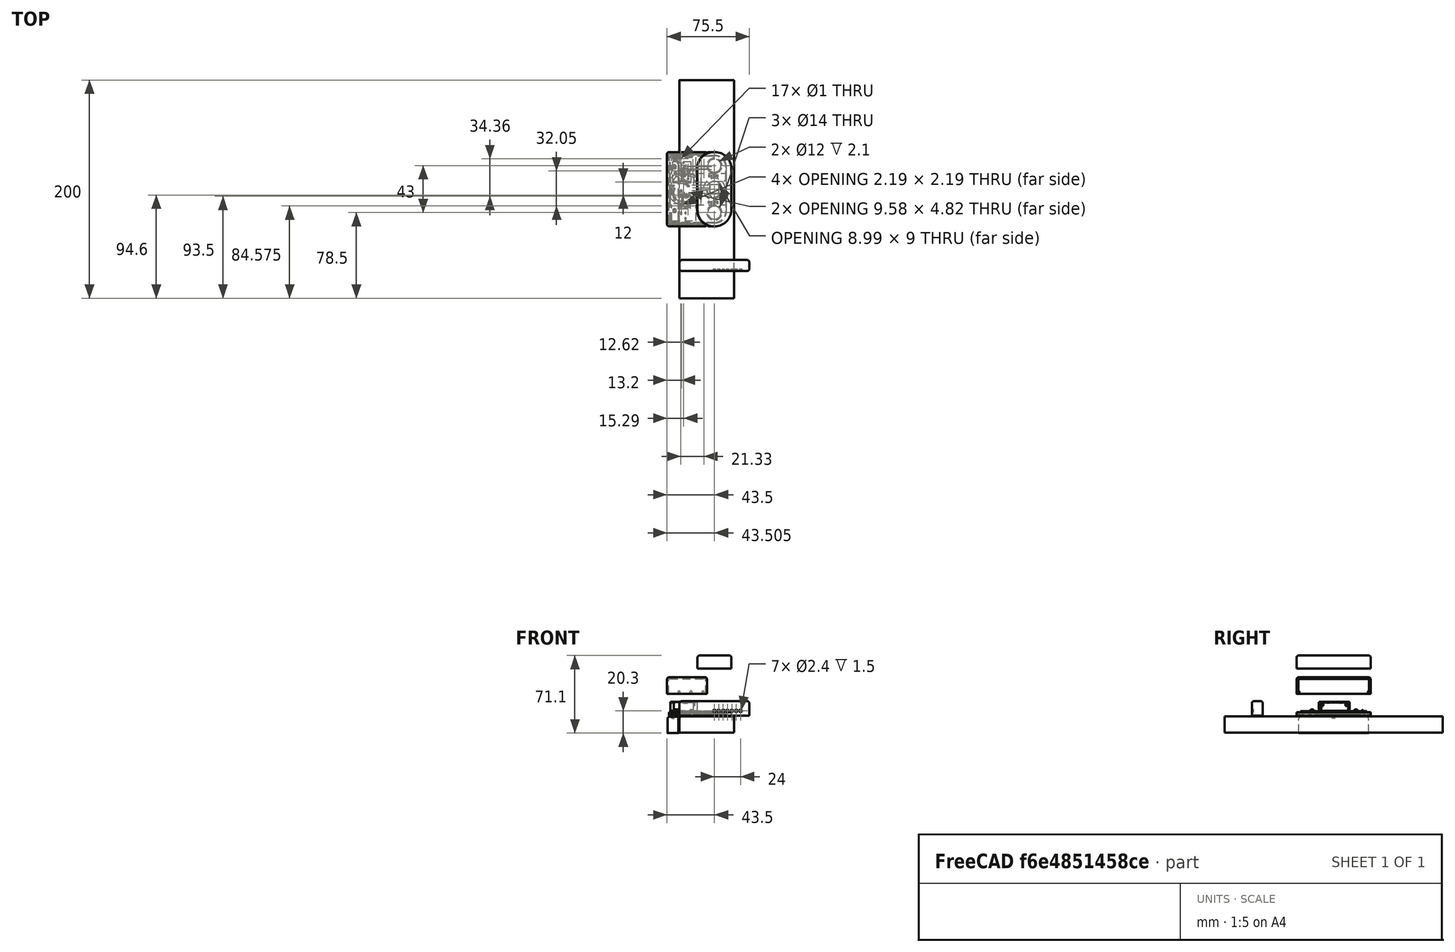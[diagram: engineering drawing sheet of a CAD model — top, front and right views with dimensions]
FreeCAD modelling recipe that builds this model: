
FCSTD DOCUMENT  (FreeCAD 0.18R4 (GitTag))
Label: RHS_3
License: All rights reserved
LicenseURL: http://en.wikipedia.org/wiki/All_rights_reserved
objects: Part::Box×15, Part::Cylinder×13, Part::Cut×13, Part::Fillet×11, Part::FeaturePython×9, Part::MultiFuse×7, Part::Sphere×2, Part::Torus×1, Part::Feature×1, Spreadsheet::Sheet×1
note: 72 computed .brp shape members not serialized (recipe doc carries the construction recipe); baked Part::Feature solids carry a one-line shape summary decoded from their .brp

FEATURE [Part::Box] Box014  label="Würfel003"
  AttacherType = Attacher::AttachEngine3D
  Height = 15
  Length = 64
  Placement = pos=(-32,-55,-1.4) rot=(0,0,1;0rad)
  Width = 10
  expr: Placement.Base.y = -Width / 2 - 50mm
  expr: Placement.Base.x = -Length / 2
FEATURE [Part::Cylinder] Cylinder004  label="Zylinder002"
  Angle = 360
  AttacherType = Attacher::AttachEngine3D
  Height = 1.8
  Placement = pos=(0,-50,11.9) rot=(0,0,1;0rad)
  Radius = 1.2
  expr: Placement.Base.z = 12.9 - 1
FEATURE [Part::FeaturePython] Array006  # Draft array (typed FeaturePython)
  Angle = 360
  ArrayType = 0
  Axis = (0,0,1)
  Base = -> Cylinder004
  Center = (0,0,0)
  Fuse = false
  IntervalAxis = (0,0,0)
  IntervalX = (4,0,0)
  IntervalY = (0,1,0)
  IntervalZ = (0,0,0)
  NumberPolar = 1
  NumberX = 1
  NumberY = 1
  NumberZ = 1
FEATURE [Part::Fillet] Fillet005
  Base = -> Box014
  Edges = 8 edges r=2: [Edge1,Edge2,Edge3,Edge5,Edge6,Edge7,Edge10,Edge12]
FEATURE [Part::Cut] Cut009  label="Unterteil"
  Base = -> Fillet005
  Placement = pos=(-88,0,-16) rot=(0,0,1;1.5708rad)
  Tool = -> Array006
  expr: Placement.Base.z = FBox.Placement.Base.z + 1mm
FEATURE [Part::Box] Box015  label="Würfel004"
  AttacherType = Attacher::AttachEngine3D
  Height = 13.2
  Length = 64
  Placement = pos=(-32,-75,-1.4) rot=(0,0,1;0rad)
  Width = 10
  expr: Placement.Base.z = Würfel003.Placement.Base.z
  expr: Height = 13.2mm
  expr: Placement.Base.y = Würfel003.Placement.Base.y - 20mm
  expr: Placement.Base.x = Würfel003.Placement.Base.x
  expr: Width = Würfel003.Width
  expr: Length = Würfel003.Length
FEATURE [Part::Cylinder] Cylinder005  label="Zylinder003"
  Angle = 360
  AttacherType = Attacher::AttachEngine3D
  Height = 1.8
  Placement = pos=(0,-73.5,2.9) rot=(1,0,0;1.5708rad)
  Radius = 1.2
  expr: Placement.Base.z = Zylinder002.Placement.Base.z - 9mm
  expr: Height = Zylinder002.Height
  expr: Placement.Base.y = Würfel004.Placement.Base.y + 1.5mm
  expr: Placement.Base.x = Zylinder002.Placement.Base.x
  expr: Radius = Zylinder002.Radius
FEATURE [Part::Fillet] Fillet006
  Base = -> Box015
  Edges = 8 edges r=2: [Edge1,Edge2,Edge3,Edge5,Edge6,Edge7,Edge10,Edge12]
FEATURE [Part::FeaturePython] Array007  # Draft array (typed FeaturePython)
  Angle = 360
  ArrayType = 0
  Axis = (0,0,1)
  Base = -> Cylinder005
  Center = (0,0,0)
  Fuse = false
  IntervalAxis = (0,0,0)
  IntervalX = (4,0,0)
  IntervalY = (0,1,0)
  IntervalZ = (0,0,0)
  NumberPolar = 1
  NumberX = 7
  NumberY = 1
  NumberZ = 1
FEATURE [Part::Cut] Cut010  label="Seitenteil"
  Base = -> Fillet006
  Tool = -> Array007
FEATURE [Part::Box] Box016  label="Vierkant"
  AttacherType = Attacher::AttachEngine3D
  Height = 10
  Length = 8
  Placement = pos=(-4,-4,-2) rot=(0,0,1;0rad)
  Width = 8
  expr: Placement.Base.y = -Width / 2
  expr: Placement.Base.x = -Length / 2
FEATURE [Part::Cylinder] Cylinder012  label="MagHoldBase"
  Angle = 360
  AttacherType = Attacher::AttachEngine3D
  Height = 2.4
  Radius = 7.7
  expr: Height = Parameter.Pcb_Height + 1.4mm
FEATURE [Part::Cylinder] Cylinder003  label="MagHoldTop"
  Angle = 360
  AttacherType = Attacher::AttachEngine3D
  Height = 1.4
  Radius = 10
  expr: Placement.Base.z = 0
FEATURE [Part::Cylinder] Cylinder013  label="Cylinder012"
  Angle = 360
  AttacherType = Attacher::AttachEngine3D
  Height = 10
  Placement = pos=(4,4,-2) rot=(0,0,1;0rad)
  Radius = 0.5
  expr: Placement.Base.y = Vierkant.Width / 2
  expr: Placement.Base.x = Vierkant.Length / 2
FEATURE [Part::FeaturePython] Array013  # Draft array (typed FeaturePython)
  Angle = 360
  ArrayType = 0
  Axis = (0,0,1)
  Base = -> Cylinder013
  Center = (0,0,0)
  Fuse = false
  IntervalAxis = (0,0,0)
  IntervalX = (-8,0,0)
  IntervalY = (0,-8,0)
  IntervalZ = (0,0,1)
  NumberPolar = 1
  NumberX = 2
  NumberY = 2
  NumberZ = 1
  expr: IntervalY.y = -Vierkant.Width
  expr: IntervalX.x = -Vierkant.Length
FEATURE [Part::Cylinder] Cylinder014  label="Magnet"
  Angle = 360
  AttacherType = Attacher::AttachEngine3D
  Height = 3
  Placement = pos=(0,-8.5,-1) rot=(0,0,1;0rad)
  Radius = 1.2
  expr: Placement.Base.z = MagHoldTop.Placement.Base.z - 1mm
  expr: Placement.Base.y = -MagHoldTop.Radius + 1.5mm
FEATURE [Part::Torus] Torus
  Angle1 = -180
  Angle2 = 180
  Angle3 = 360
  AttacherType = Attacher::AttachEngine3D
  Placement = pos=(0,0,1.9) rot=(0,0,1;0rad)
  Radius1 = 7.7
  Radius2 = 0.7
  expr: Radius1 = MagHoldBase.Radius
FEATURE [Part::Cut] Cut017
  Base = -> Cylinder012
  Tool = -> Torus
FEATURE [Part::MultiFuse] Fusion003
  Shapes = -> [Cylinder003,Cut017]
FEATURE [Part::Cut] Cut018
  Base = -> Fusion003
  Tool = -> Box016
FEATURE [Part::Cut] Cut019
  Base = -> Cut018
  Tool = -> Array013
FEATURE [Part::Cut] Cut020  label="MagnetHalter"
  Base = -> Cut019
  Tool = -> Cylinder014
  expr: Placement.Base.z = 0mm + 0mm
FEATURE [Part::Box] Box018  label="Cube"
  AttacherType = Attacher::AttachEngine3D
  Height = 12
  Length = 31
  Placement = pos=(-15.5,-34,1.7) rot=(0,0,1;0rad)
  Width = 68
  expr: Length = Parameter.GriffR_Width
  expr: Width = Parameter.GriffR_Height
  expr: Placement.Base.z = ERO.Placement.Base.z + ERO.Height
  expr: Placement.Base.y = -Width / 2
  expr: Placement.Base.x = -Length / 2
FEATURE [Part::Fillet] Fillet010  label="GriffBaseR"
  Base = -> Box018
  Edges = 4 edges r=15: [Edge1,Edge3,Edge5,Edge7]
FEATURE [Part::Fillet] Fillet011  label="GriffR"
  Base = -> Fillet010
  Edges = 8 edges r=2: [Edge1,Edge5,Edge6,Edge7,Edge8,Edge9,Edge10,Edge11]
  Placement = pos=(0,0,40) rot=(0,0,1;0rad)
FEATURE [Part::Box] Box019  label="DBlockR"
  AttacherType = Attacher::AttachEngine3D
  Height = 15.1
  Length = 37
  Placement = pos=(-43.5,-34,-1.4) rot=(0,0,1;0rad)
  Width = 68
  expr: Height = ERO.Height + 12mm
  expr: Placement.Base.z = ERO.Placement.Base.z
  expr: Placement.Base.y = -Width / 2
  expr: Placement.Base.x = RR.Placement.Base.x
  expr: Width = Parameter.GriffR_Height
FEATURE [Part::FeaturePython] Clone003  label="GriffBaseRForCut"  # Draft clone (typed FeaturePython)
  AttacherType = Attacher::AttachEngine3D
  Fuse = false
  Objects = -> [Fillet010]
  Placement = pos=(0,0,-5) rot=(0,0,1;0rad)
  Scale = (1.02,1.01,1.8)
FEATURE [Part::Fillet] Fillet012
  Base = -> Box019
  Edges = 8 edges r=2: [Edge1,Edge2,Edge3,Edge5,Edge6,Edge7,Edge10,Edge12]
FEATURE [Part::Cut] Cut024
  Base = -> Fillet012
  Tool = -> Clone003
FEATURE [Part::Box] Box020  label="DBlockRCutout"
  AttacherType = Attacher::AttachEngine3D
  Height = 13.5
  Length = 37
  Placement = pos=(-41.9,-32.4,-1.4) rot=(0,0,1;0rad)
  Width = 64.8
  expr: Placement.Base.y = -Width / 2
  expr: Placement.Base.x = DBlockR.Placement.Base.x + Parameter.Wall_Width
  expr: Placement.Base.z = DBlockR.Placement.Base.z
  expr: Height = DBlockR.Height - Parameter.Wall_Width
  expr: Width = DBlockR.Width - Parameter.Wall_Width - Parameter.Wall_Width
  expr: Length = DBlockR.Length
FEATURE [Part::Fillet] Fillet013
  Base = -> Box020
  Edges = 2 edges r=1: [Edge1,Edge3]
FEATURE [Part::Cut] Cut025
  Base = -> Cut024
  Tool = -> Fillet013
FEATURE [Part::Cylinder] Cylinder017  label="CR2477"
  Angle = 360
  AttacherType = Attacher::AttachEngine3D
  Height = 7.7
  Placement = pos=(-28,1,3) rot=(0,0,1;0rad)
  Radius = 12.25
  expr: Placement.Base.z = PlatineV_1_1.Placement.Base.z + 0.4mm
FEATURE [Part::Box] Box021  label="FBox"
  AttacherType = Attacher::AttachEngine3D
  Height = 15
  Length = 50
  Placement = pos=(-32,-100,-17) rot=(0,0,1;0rad)
  Width = 200
  expr: Placement.Base.z = -Height - 2mm
  expr: Placement.Base.x = -32
  expr: Placement.Base.y = -Width / 2
FEATURE [Part::Fillet] Fillet015  label="FensterRahmen"
  Base = -> Box021
  Edges = 1 edges r=2: [Edge2]
FEATURE [Part::Feature] RHS_3_cp_cp002  label="PlatineV_1_1"
  Placement = pos=(-100,100,2.6) rot=(0,0,1;0rad)
  shape: bbox 51 x 61 x 11.72 mm, 3088 faces, 33 solids (baked)
  expr: Placement.Base.z = 2.6mm + 0mm
FEATURE [Spreadsheet::Sheet] Spreadsheet  label="Parameter"
  cells = A3=Griff Rund; A4=Höhe; B4(GriffR_Height)==68mm; A5=Breite; B5(GriffR_Width)==31mm; C5=Rundung muss bei GriffBaseR angepasst werden; A8=Platine; A9=Dicke; B9(Pcb_Height)==1mm; A10=Bauteilhöhe; B10(Part_Height)==1.5mm; A11=Breite; B11(Pcb_Width)==51mm; A12=Länge; B12(Pcb_Length)==61mm; A13=Radius; B13(Pcb_Radius)==10.5mm; A15=Deckel; A16=Wandstärke; B16(Wall_Width)==1.6mm
FEATURE [Part::Cylinder] Cylinder018  label="ERO"
  Angle = 90
  AttacherType = Attacher::AttachEngine3D
  Height = 3.1
  Placement = pos=(0,18.5,-1.4) rot=(0,0,1;0rad)
  Radius = 15.5
  expr: Height = Parameter.Pcb_Height + Parameter.Part_Height + 0.6mm
  expr: Placement.Base.y = Parameter.GriffR_Height / 2 - Radius
  expr: Radius = Parameter.GriffR_Width / 2
FEATURE [Part::Cylinder] Cylinder019  label="ERU"
  Angle = 90
  AttacherType = Attacher::AttachEngine3D
  Height = 3.1
  Placement = pos=(0,-18.5,-1.4) rot=(0,0,-1;1.5708rad)
  Radius = 15.5
  expr: Placement.Base.z = ERO.Placement.Base.z
  expr: Height = ERO.Height
  expr: Placement.Base.y = -ERO.Placement.Base.y
  expr: Radius = ERO.Radius
FEATURE [Part::Box] Box024  label="MR"
  AttacherType = Attacher::AttachEngine3D
  Height = 3.1
  Length = 15.5
  Placement = pos=(0,-18.5,-1.4) rot=(0,0,1;0rad)
  Width = 37
  expr: Placement.Base.y = -Width / 2
  expr: Placement.Base.z = ERO.Placement.Base.z
  expr: Height = ERO.Height
  expr: Width = Parameter.GriffR_Height - Parameter.GriffR_Width
  expr: Length = ERO.Radius
FEATURE [Part::Box] Box025  label="RR"
  AttacherType = Attacher::AttachEngine3D
  Height = 3.1
  Length = 43.5
  Placement = pos=(-43.5,-34,-1.4) rot=(0,0,1;0rad)
  Width = 68
  expr: Width = Parameter.GriffR_Height
  expr: Placement.Base.z = ERO.Placement.Base.z
  expr: Height = ERO.Height
  expr: Placement.Base.y = -Width / 2
  expr: Placement.Base.x = -Length
  expr: Length = Parameter.Pcb_Width - Parameter.Pcb_Radius + 3mm
FEATURE [Part::Fillet] Fillet017
  Base = -> Box025
  Edges = 2 edges r=2: [Edge1,Edge3]
FEATURE [Part::MultiFuse] Fusion007  label="GPR"
  Shapes = -> [Cylinder018,Cylinder019,Box024,Fillet017]
FEATURE [Part::Box] Box026  label="PlatineCut"
  AttacherType = Attacher::AttachEngine3D
  Height = 1
  Length = 52
  Placement = pos=(-41,-31,0.7) rot=(0,0,1;0rad)
  Width = 62
  expr: Placement.Base.x = RR.Placement.Base.x + 2.5mm
  expr: Placement.Base.y = -Width / 2
  expr: Placement.Base.z = ERO.Placement.Base.z + ERO.Height - Height
  expr: Height = Parameter.Pcb_Height
FEATURE [Part::Fillet] Fillet018
  Base = -> Box026
  Edges = 2 edges r=2.5: [Edge1,Edge3]
FEATURE [Part::Fillet] Fillet019
  Base = -> Fillet018
  Edges = 2 edges r=10.5: [Edge17,Edge18]
FEATURE [Part::Cut] Cut030
  Base = -> Fusion007
  Tool = -> Fillet019
FEATURE [Part::Box] Box027  label="PartCut1"
  AttacherType = Attacher::AttachEngine3D
  Height = 1.5
  Length = 52
  Placement = pos=(-41,-14.5,-0.8) rot=(0,0,1;0rad)
  Width = 29
  expr: Placement.Base.y = -Width / 2
  expr: Placement.Base.x = PlatineCut.Placement.Base.x
  expr: Length = PlatineCut.Length
  expr: Placement.Base.z = PlatineCut.Placement.Base.z - Height
  expr: Height = Parameter.Part_Height
FEATURE [Part::Box] Box028  label="PartCut2"
  AttacherType = Attacher::AttachEngine3D
  Height = 1.5
  Length = 22
  Placement = pos=(-39,-29,-0.8) rot=(0,0,1;0rad)
  Width = 58
  expr: Placement.Base.y = -Width / 2
  expr: Placement.Base.x = PartCut1.Placement.Base.x + 2mm
  expr: Placement.Base.z = PartCut1.Placement.Base.z
  expr: Height = PartCut1.Height
FEATURE [Part::MultiFuse] Fusion008  label="PartCuts"
  Shapes = -> [Box027,Box028]
FEATURE [Part::Cut] Cut031
  Base = -> Cut030
  Tool = -> Fusion008
FEATURE [Part::Cylinder] Cylinder020  label="LochU"
  Angle = 360
  AttacherType = Attacher::AttachEngine3D
  Height = 10
  Placement = pos=(0,-21.5,-3) rot=(0,0,1;0rad)
  Radius = 6
FEATURE [Part::Cylinder] Cylinder021  label="LochO"
  Angle = 360
  AttacherType = Attacher::AttachEngine3D
  Height = 10
  Placement = pos=(0,21.5,-3) rot=(0,0,1;0rad)
  Radius = 6
  expr: Placement.Base.y = -LochU.Placement.Base.y
  expr: Placement.Base.z = LochU.Placement.Base.z
FEATURE [Part::Cylinder] Cylinder022  label="LochM"
  Angle = 360
  AttacherType = Attacher::AttachEngine3D
  Height = 10
  Placement = pos=(0,0,-3) rot=(0,0,1;0rad)
  Radius = 7
  expr: Placement.Base.z = LochU.Placement.Base.z
FEATURE [Part::MultiFuse] Fusion009  label="LochOMU"
  Shapes = -> [Cylinder020,Cylinder021,Cylinder022]
FEATURE [Part::Cut] Cut032
  Base = -> Cut031
  Tool = -> Fusion009
FEATURE [Part::Box] Box029  label="DBCut"
  AttacherType = Attacher::AttachEngine3D
  Height = 10
  Length = 37
  Placement = pos=(-43.5,-34,-1.4) rot=(0,0,1;0rad)
  Width = 1.8
  expr: Width = Parameter.Wall_Width + 0.2mm
  expr: Placement.Base.z = DBlockR.Placement.Base.z
  expr: Placement.Base.y = DBlockR.Placement.Base.y
  expr: Placement.Base.x = DBlockR.Placement.Base.x
  expr: Length = DBlockR.Length
FEATURE [Part::FeaturePython] Array016  # Draft array (typed FeaturePython)
  Angle = 360
  ArrayType = 0
  Axis = (0,0,1)
  Base = -> Box029
  Center = (0,0,0)
  Fuse = false
  IntervalAxis = (0,0,0)
  IntervalX = (1,0,0)
  IntervalY = (0,66.2,0)
  IntervalZ = (0,0,1)
  NumberPolar = 1
  NumberX = 1
  NumberY = 2
  NumberZ = 1
  expr: IntervalY.y = DBlockR.Width - DBCut.Width
FEATURE [Part::Box] Box030  label="DBCut2"
  AttacherType = Attacher::AttachEngine3D
  Height = 10
  Length = 1.8
  Placement = pos=(-43.5,-34,-1.4) rot=(0,0,1;0rad)
  Width = 68
  expr: Placement.Base.z = DBlockR.Placement.Base.z
  expr: Placement.Base.y = DBlockR.Placement.Base.y
  expr: Placement.Base.x = DBlockR.Placement.Base.x
  expr: Width = DBlockR.Width
  expr: Length = DBCut.Width
FEATURE [Part::MultiFuse] Fusion012  label="DeckelRandCut"
  Shapes = -> [Array016,Box030]
FEATURE [Part::Cut] Cut033
  Base = -> Cut032
  Tool = -> Fusion012
FEATURE [Part::Fillet] Fillet020
  Base = -> Cut033
  Edges = 4 edges r=1: [Edge12,Edge91,Edge93,Edge94]
FEATURE [Part::Sphere] Sphere  label="Fed0"
  Angle1 = -90
  Angle2 = 90
  Angle3 = 360
  AttacherType = Attacher::AttachEngine3D
  Placement = pos=(-10.5,-32.4,0.2) rot=(0,0,1;0rad)
  Radius = 1
  expr: Placement.Base.z = DBlockR.Placement.Base.z + Radius + 0.6mm
  expr: Placement.Base.x = DBlockR.Placement.Base.x + DBlockR.Length - 4mm
  expr: Placement.Base.y = DBlockR.Placement.Base.y + Parameter.Wall_Width
FEATURE [Part::FeaturePython] Array  label="FedAll"  # Draft array (typed FeaturePython)
  Angle = 360
  ArrayType = 0
  Axis = (0,0,1)
  Base = -> Sphere
  Center = (0,0,0)
  Fuse = false
  IntervalAxis = (0,0,0)
  IntervalX = (-11,0,0)
  IntervalY = (0,64.8,0)
  IntervalZ = (0,0,1)
  NumberPolar = 1
  NumberX = 3
  NumberY = 2
  NumberZ = 1
  expr: IntervalY.y = DBlockRCutout.Width
FEATURE [Part::MultiFuse] Fusion  label="DeckelR"
  Placement = pos=(0,0,20) rot=(0,0,1;0rad)
  Shapes = -> [Cut025,Array]
FEATURE [Part::Sphere] Sphere001  label="Nut0"
  Angle1 = -90
  Angle2 = 90
  Angle3 = 360
  AttacherType = Attacher::AttachEngine3D
  Placement = pos=(-10.5,-32.4,0.2) rot=(0,0,1;0rad)
  Radius = 1.1
  expr: Placement.Base.z = Fed0.Placement.Base.z
  expr: Placement.Base.y = Fed0.Placement.Base.y
  expr: Placement.Base.x = Fed0.Placement.Base.x
  expr: Radius = Fed0.Radius + 0.1mm
FEATURE [Part::FeaturePython] Array017  label="Nut01"  # Draft array (typed FeaturePython)
  Angle = 360
  ArrayType = 0
  Axis = (0,0,1)
  Base = -> Sphere001
  Center = (0,0,0)
  Fuse = false
  IntervalAxis = (0,0,0)
  IntervalX = (-3,0,0)
  IntervalY = (0,64.8,0)
  IntervalZ = (0,0,1)
  NumberPolar = 1
  NumberX = 2
  NumberY = 2
  NumberZ = 1
  expr: IntervalY.y = FedAll.IntervalY.y
FEATURE [Part::Cylinder] Cylinder  label="Nut1"
  Angle = 360
  AttacherType = Attacher::AttachEngine3D
  Height = 27
  Placement = pos=(-40.5,-32.4,0.2) rot=(0,1,0;1.5708rad)
  Radius = 1.1
  expr: Placement.Base.z = Nut0.Placement.Base.z
  expr: Placement.Base.y = Nut0.Placement.Base.y
  expr: Placement.Base.x = Nut0.Placement.Base.x + Nut01.IntervalX.x - Height
  expr: Radius = Nut0.Radius
FEATURE [Part::FeaturePython] Array018  # Draft array (typed FeaturePython)
  Angle = 360
  ArrayType = 0
  Axis = (0,0,1)
  Base = -> Cylinder
  Center = (0,0,0)
  Fuse = false
  IntervalAxis = (0,0,0)
  IntervalX = (1,0,0)
  IntervalY = (0,64.8,0)
  IntervalZ = (0,0,1)
  NumberPolar = 1
  NumberX = 1
  NumberY = 2
  NumberZ = 1
  expr: IntervalY.y = FedAll.IntervalY.y
FEATURE [Part::Box] Box  label="NutIn"
  AttacherType = Attacher::AttachEngine3D
  Height = 10
  Length = 5
  Placement = pos=(-18.5,-33.5,0.2) rot=(0,0,1;0rad)
  Width = 2.6
  expr: Placement.Base.z = Nut0.Placement.Base.z
  expr: Placement.Base.y = Nut0.Placement.Base.y - Nut0.Radius
  expr: Placement.Base.x = Nut0.Placement.Base.x - Length - 3mm
  expr: Width = Nut0.Radius * 2 + 0.4mm
FEATURE [Part::FeaturePython] Array019  # Draft array (typed FeaturePython)
  Angle = 360
  ArrayType = 0
  Axis = (0,0,1)
  Base = -> Box
  Center = (0,0,0)
  Fuse = false
  IntervalAxis = (0,0,0)
  IntervalX = (-11,0,0)
  IntervalY = (0,64.8,0)
  IntervalZ = (0,0,1)
  NumberPolar = 1
  NumberX = 3
  NumberY = 2
  NumberZ = 1
  expr: IntervalY.y = FedAll.IntervalY.y
  expr: IntervalX.x = FedAll.IntervalX.x
FEATURE [Part::MultiFuse] Fusion013  label="NutAll"
  Shapes = -> [Array017,Array018,Array019]
FEATURE [Part::Cut] Cut  label="BodenR"
  Base = -> Fillet020
  Tool = -> Fusion013
